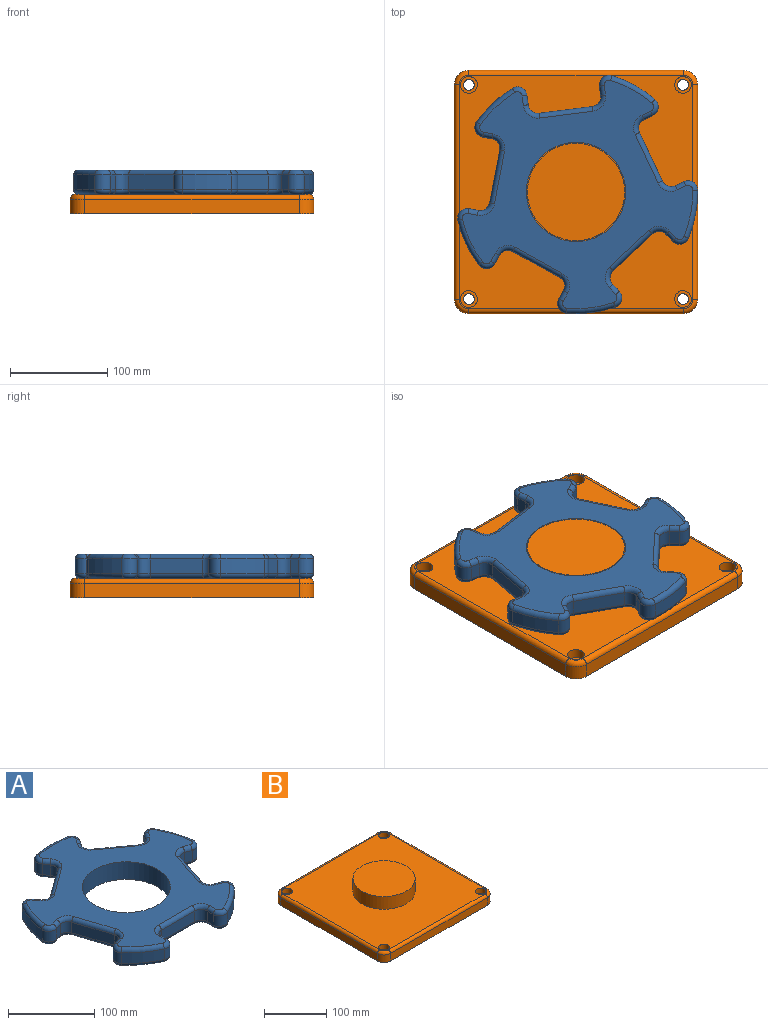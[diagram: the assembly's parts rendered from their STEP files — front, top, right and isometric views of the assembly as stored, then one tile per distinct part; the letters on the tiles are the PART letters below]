
ASSEMBLY  parts=2 mates=1
PART A: 123 faces, bbox 268.9x258.5x25 mm
  f0: plane 238.57x229.73mm, normal (0,0,1), area 21505.7mm2, adj f6,f43,f44,f45,f46,f47,f48,f49
  f1: plane 238.57x229.73mm, normal (0,0,-1), area 21505.7mm2, adj f6,f83,f84,f85,f86,f87,f88,f89
  f2: cylinder r=125mm len=40.68mm, axis (0,0,-1), area 759.5mm2, adj f13,f42,f51,f91
  f3: cylinder r=125mm len=47.82mm, axis (0,0,-1), area 759.5mm2, adj f35,f41,f67,f107
  f4: cylinder r=125mm len=50.29mm, axis (0,0,-1), area 759.5mm2, adj f28,f34,f82,f122
  f5: cylinder r=125mm len=47.82mm, axis (0,0,-1), area 759.5mm2, adj f21,f27,f66,f106
  f6: cylinder r=51mm len=102mm, axis (0,0,-1), area 8011.1mm2, adj f0,f1
  f7: cylinder r=125mm len=40.68mm, axis (0,0,-1), area 759.5mm2, adj f14,f20,f50,f90
  f8: plane 15x9.73mm, normal (-1,0,0), area 146mm2, adj f11,f14,f46,f86
  f9: plane 55x15mm, normal (0,-1,0), area 825mm2, adj f11,f12,f43,f83
  f10: plane 15x9.73mm, normal (1,0,0), area 146mm2, adj f12,f13,f47,f87
  f11: cylinder r=10mm len=15mm, axis (0,0,-1), area 235.6mm2, adj f8,f9,f44,f84
  f12: cylinder r=10mm len=15mm, axis (0,0,-1), area 235.6mm2, adj f9,f10,f45,f85
  f13: cylinder r=10mm len=15mm, axis (0,0,-1), area 299.5mm2, adj f2,f10,f49,f89
  f14: cylinder r=10mm len=15mm, axis (0,0,-1), area 299.5mm2, adj f7,f8,f48,f88
  f15: plane 15x9.26mm, normal (-0.31,-0.95,0), area 146mm2, adj f18,f21,f62,f102
  f16: plane 52.31x17mm, normal (0.95,-0.31,0), area 825mm2, adj f18,f19,f58,f98
  f17: plane 15x9.26mm, normal (0.31,0.95,0), area 146mm2, adj f19,f20,f54,f94
  f18: cylinder r=10mm len=15mm, axis (0,0,-1), area 235.6mm2, adj f15,f16,f60,f100
  f19: cylinder r=10mm len=15mm, axis (0,0,-1), area 235.6mm2, adj f16,f17,f56,f96
  f20: cylinder r=10mm len=16.25mm, axis (0,0,-1), area 299.5mm2, adj f7,f17,f52,f92
  f21: cylinder r=10mm len=15mm, axis (0,0,-1), area 299.5mm2, adj f5,f15,f64,f104
  f22: plane 15x7.87mm, normal (0.81,-0.59,0), area 146mm2, adj f25,f28,f78,f118
  f23: plane 44.5x32.33mm, normal (0.59,0.81,0), area 825mm2, adj f25,f26,f74,f114
  f24: plane 15x7.87mm, normal (-0.81,0.59,0), area 146mm2, adj f26,f27,f70,f110
  f25: cylinder r=10mm len=15mm, axis (0,0,-1), area 235.6mm2, adj f22,f23,f76,f116
  f26: cylinder r=10mm len=15mm, axis (0,0,-1), area 235.6mm2, adj f23,f24,f72,f112
  f27: cylinder r=10mm len=16.78mm, axis (0,0,-1), area 299.5mm2, adj f5,f24,f68,f108
  f28: cylinder r=10mm len=15.67mm, axis (0,0,-1), area 299.5mm2, adj f4,f22,f80,f120
  f29: plane 15x7.87mm, normal (0.81,0.59,0), area 146mm2, adj f32,f35,f71,f111
  f30: plane 44.5x32.33mm, normal (-0.59,0.81,0), area 825mm2, adj f32,f33,f75,f115
  f31: plane 15x7.87mm, normal (-0.81,-0.59,0), area 146mm2, adj f33,f34,f79,f119
  f32: cylinder r=10mm len=15mm, axis (0,0,-1), area 235.6mm2, adj f29,f30,f73,f113
  f33: cylinder r=10mm len=15mm, axis (0,0,-1), area 235.6mm2, adj f30,f31,f77,f117
  f34: cylinder r=10mm len=15.67mm, axis (0,0,-1), area 299.5mm2, adj f4,f31,f81,f121
  f35: cylinder r=10mm len=16.78mm, axis (0,0,-1), area 299.5mm2, adj f3,f29,f69,f109
  f36: plane 15x9.26mm, normal (-0.31,0.95,0), area 146mm2, adj f39,f42,f55,f95
  f37: plane 52.31x17mm, normal (-0.95,-0.31,0), area 825mm2, adj f39,f40,f59,f99
  f38: plane 15x9.26mm, normal (0.31,-0.95,0), area 146mm2, adj f40,f41,f63,f103
  f39: cylinder r=10mm len=15mm, axis (0,0,-1), area 235.6mm2, adj f36,f37,f57,f97
  f40: cylinder r=10mm len=15mm, axis (0,0,-1), area 235.6mm2, adj f37,f38,f61,f101
  f41: cylinder r=10mm len=15mm, axis (0,0,-1), area 299.5mm2, adj f3,f38,f65,f105
  f42: cylinder r=10mm len=16.25mm, axis (0,0,-1), area 299.5mm2, adj f2,f36,f53,f93
  f43: cylinder r=5mm len=55mm, axis (1,0,0), area 432mm2, adj f0,f9,f44,f45
  f44: torus R=15mm, axis (0,0,1), area 145.8mm2, adj f0,f11,f43,f46
  f45: torus R=15mm, axis (0,0,1), area 145.8mm2, adj f0,f12,f43,f47
  f46: cylinder r=5mm len=9.73mm, axis (0,-1,0), area 76.4mm2, adj f0,f8,f44,f48
  f47: cylinder r=5mm len=9.73mm, axis (0,1,0), area 76.4mm2, adj f0,f10,f45,f49
  f48: torus R=5mm, axis (0,0,1), area 128.3mm2, adj f0,f14,f46,f50
  f49: torus R=5mm, axis (0,0,1), area 128.3mm2, adj f0,f13,f47,f51
  f50: torus R=120mm, axis (0,0,1), area 391.9mm2, adj f0,f7,f48,f52
  f51: torus R=120mm, axis (0,0,1), area 391.9mm2, adj f0,f2,f49,f53
  f52: torus R=5mm, axis (0,0,1), area 128.3mm2, adj f0,f20,f50,f54
  f53: torus R=5mm, axis (0,0,1), area 128.3mm2, adj f0,f42,f51,f55
  f54: cylinder r=5mm len=10.8mm, axis (-0.95,0.31,0), area 76.4mm2, adj f0,f17,f52,f56
  f55: cylinder r=5mm len=10.8mm, axis (-0.95,-0.31,0), area 76.4mm2, adj f0,f36,f53,f57
  f56: torus R=15mm, axis (0,0,1), area 145.8mm2, adj f0,f19,f54,f58
  f57: torus R=15mm, axis (0,0,1), area 145.8mm2, adj f0,f39,f55,f59
  f58: cylinder r=5mm len=53.85mm, axis (0.31,0.95,0), area 432mm2, adj f0,f16,f56,f60
  f59: cylinder r=5mm len=53.85mm, axis (0.31,-0.95,0), area 432mm2, adj f0,f37,f57,f61
  f60: torus R=15mm, axis (0,0,1), area 145.8mm2, adj f0,f18,f58,f62
  f61: torus R=15mm, axis (0,0,1), area 145.8mm2, adj f0,f40,f59,f63
  f62: cylinder r=5mm len=10.8mm, axis (0.95,-0.31,0), area 76.4mm2, adj f0,f15,f60,f64
  f63: cylinder r=5mm len=10.8mm, axis (0.95,0.31,0), area 76.4mm2, adj f0,f38,f61,f65
  f64: torus R=5mm, axis (0,0,1), area 128.3mm2, adj f0,f21,f62,f66
  f65: torus R=5mm, axis (0,0,1), area 128.3mm2, adj f0,f41,f63,f67
  f66: torus R=120mm, axis (0,0,1), area 391.9mm2, adj f0,f5,f64,f68
  f67: torus R=120mm, axis (0,0,1), area 391.9mm2, adj f0,f3,f65,f69
  f68: torus R=5mm, axis (0,0,1), area 128.3mm2, adj f0,f27,f66,f70
  f69: torus R=5mm, axis (0,0,1), area 128.3mm2, adj f0,f35,f67,f71
  f70: cylinder r=5mm len=10.81mm, axis (-0.59,-0.81,0), area 76.4mm2, adj f0,f24,f68,f72
  f71: cylinder r=5mm len=10.81mm, axis (-0.59,0.81,0), area 76.4mm2, adj f0,f29,f69,f73
  f72: torus R=15mm, axis (0,0,1), area 145.8mm2, adj f0,f26,f70,f74
  f73: torus R=15mm, axis (0,0,1), area 145.8mm2, adj f0,f32,f71,f75
  f74: cylinder r=5mm len=47.44mm, axis (-0.81,0.59,0), area 432mm2, adj f0,f23,f72,f76
  f75: cylinder r=5mm len=47.44mm, axis (-0.81,-0.59,0), area 432mm2, adj f0,f30,f73,f77
  f76: torus R=15mm, axis (0,0,1), area 145.8mm2, adj f0,f25,f74,f78
  f77: torus R=15mm, axis (0,0,1), area 145.8mm2, adj f0,f33,f75,f79
  f78: cylinder r=5mm len=10.81mm, axis (0.59,0.81,0), area 76.4mm2, adj f0,f22,f76,f80
  f79: cylinder r=5mm len=10.81mm, axis (0.59,-0.81,0), area 76.4mm2, adj f0,f31,f77,f81
  f80: torus R=5mm, axis (0,0,1), area 128.3mm2, adj f0,f28,f78,f82
  f81: torus R=5mm, axis (0,0,1), area 128.3mm2, adj f0,f34,f79,f82
  f82: torus R=120mm, axis (0,0,1), area 391.9mm2, adj f0,f4,f80,f81
  f83: cylinder r=5mm len=55mm, axis (-1,0,0), area 432mm2, adj f1,f9,f84,f85
  f84: torus R=15mm, axis (0,0,1), area 145.8mm2, adj f1,f11,f83,f86
  f85: torus R=15mm, axis (0,0,1), area 145.8mm2, adj f1,f12,f83,f87
  f86: cylinder r=5mm len=9.73mm, axis (0,1,0), area 76.4mm2, adj f1,f8,f84,f88
  f87: cylinder r=5mm len=9.73mm, axis (0,-1,0), area 76.4mm2, adj f1,f10,f85,f89
  f88: torus R=5mm, axis (0,0,1), area 128.3mm2, adj f1,f14,f86,f90
  f89: torus R=5mm, axis (0,0,1), area 128.3mm2, adj f1,f13,f87,f91
  f90: torus R=120mm, axis (0,0,1), area 391.9mm2, adj f1,f7,f88,f92
  f91: torus R=120mm, axis (0,0,1), area 391.9mm2, adj f1,f2,f89,f93
  f92: torus R=5mm, axis (0,0,1), area 128.3mm2, adj f1,f20,f90,f94
  f93: torus R=5mm, axis (0,0,1), area 128.3mm2, adj f1,f42,f91,f95
  f94: cylinder r=5mm len=10.8mm, axis (0.95,-0.31,0), area 76.4mm2, adj f1,f17,f92,f96
  f95: cylinder r=5mm len=10.8mm, axis (0.95,0.31,0), area 76.4mm2, adj f1,f36,f93,f97
  f96: torus R=15mm, axis (0,0,1), area 145.8mm2, adj f1,f19,f94,f98
  f97: torus R=15mm, axis (0,0,1), area 145.8mm2, adj f1,f39,f95,f99
  f98: cylinder r=5mm len=53.85mm, axis (-0.31,-0.95,0), area 432mm2, adj f1,f16,f96,f100
  f99: cylinder r=5mm len=53.85mm, axis (-0.31,0.95,0), area 432mm2, adj f1,f37,f97,f101
  f100: torus R=15mm, axis (0,0,1), area 145.8mm2, adj f1,f18,f98,f102
  f101: torus R=15mm, axis (0,0,1), area 145.8mm2, adj f1,f40,f99,f103
  f102: cylinder r=5mm len=10.8mm, axis (-0.95,0.31,0), area 76.4mm2, adj f1,f15,f100,f104
  f103: cylinder r=5mm len=10.8mm, axis (-0.95,-0.31,0), area 76.4mm2, adj f1,f38,f101,f105
  f104: torus R=5mm, axis (0,0,1), area 128.3mm2, adj f1,f21,f102,f106
  f105: torus R=5mm, axis (0,0,1), area 128.3mm2, adj f1,f41,f103,f107
  f106: torus R=120mm, axis (0,0,1), area 391.9mm2, adj f1,f5,f104,f108
  f107: torus R=120mm, axis (0,0,1), area 391.9mm2, adj f1,f3,f105,f109
  f108: torus R=5mm, axis (0,0,1), area 128.3mm2, adj f1,f27,f106,f110
  f109: torus R=5mm, axis (0,0,1), area 128.3mm2, adj f1,f35,f107,f111
  f110: cylinder r=5mm len=10.81mm, axis (0.59,0.81,0), area 76.4mm2, adj f1,f24,f108,f112
  f111: cylinder r=5mm len=10.81mm, axis (0.59,-0.81,0), area 76.4mm2, adj f1,f29,f109,f113
  f112: torus R=15mm, axis (0,0,1), area 145.8mm2, adj f1,f26,f110,f114
  f113: torus R=15mm, axis (0,0,1), area 145.8mm2, adj f1,f32,f111,f115
  f114: cylinder r=5mm len=47.44mm, axis (0.81,-0.59,0), area 432mm2, adj f1,f23,f112,f116
  f115: cylinder r=5mm len=47.44mm, axis (0.81,0.59,0), area 432mm2, adj f1,f30,f113,f117
  f116: torus R=15mm, axis (0,0,1), area 145.8mm2, adj f1,f25,f114,f118
  f117: torus R=15mm, axis (0,0,1), area 145.8mm2, adj f1,f33,f115,f119
  f118: cylinder r=5mm len=10.81mm, axis (-0.59,-0.81,0), area 76.4mm2, adj f1,f22,f116,f120
  f119: cylinder r=5mm len=10.81mm, axis (-0.59,0.81,0), area 76.4mm2, adj f1,f31,f117,f121
  f120: torus R=5mm, axis (0,0,1), area 128.3mm2, adj f1,f28,f118,f122
  f121: torus R=5mm, axis (0,0,1), area 128.3mm2, adj f1,f34,f119,f122
  f122: torus R=120mm, axis (0,0,1), area 391.9mm2, adj f1,f4,f120,f121
PART B: 32 faces, bbox 252.5x252.5x45 mm
  f0: plane 220x15mm, normal (1,0,0), area 3300mm2, adj f5,f8,f11,f27
  f1: plane 220x15mm, normal (0,1,0), area 3300mm2, adj f5,f8,f9,f31
  f2: plane 220x15mm, normal (-1,0,0), area 3300mm2, adj f5,f9,f10,f28
  f3: plane 220x15mm, normal (0,-1,0), area 3300mm2, adj f5,f10,f11,f24
  f4: plane 240x240mm, normal (0,0,1), area 48725.4mm2, adj f6,f14,f17,f20,f23,f24,f25,f26
  f5: plane 250x250mm, normal (0,0,-1), area 61926.7mm2, adj f0,f1,f2,f3,f8,f9,f10,f11
  f6: cylinder r=50mm len=100mm, axis (0,0,-1), area 7854mm2, adj f4,f7
  f7: plane 100x100mm, normal (0,0,1), area 7854mm2, adj f6
  f8: cylinder r=15mm len=15mm, axis (0,0,-1), area 353.4mm2, adj f0,f1,f5,f29
  f9: cylinder r=15mm len=15mm, axis (0,0,1), area 353.4mm2, adj f1,f2,f5,f30
  f10: cylinder r=15mm len=15mm, axis (0,0,-1), area 353.4mm2, adj f2,f3,f5,f26
  f11: cylinder r=15mm len=15mm, axis (0,0,1), area 353.4mm2, adj f0,f3,f5,f25
  f12: cylinder r=5.5mm len=11mm, axis (0,0,1), area 345.6mm2, adj f5,f13
  f13: plane 17.25x17.25mm, normal (0,0,1), area 138.7mm2, adj f12,f14
  f14: cylinder r=8.62mm len=17.25mm, axis (0,0,1), area 541.9mm2, adj f4,f13
  f15: cylinder r=5.5mm len=11mm, axis (0,0,1), area 345.6mm2, adj f5,f16
  f16: plane 17.25x17.25mm, normal (0,0,1), area 138.7mm2, adj f15,f17
  f17: cylinder r=8.62mm len=17.25mm, axis (0,0,1), area 541.9mm2, adj f4,f16
  f18: cylinder r=5.5mm len=11mm, axis (0,0,1), area 345.6mm2, adj f5,f19
  f19: plane 17.25x17.25mm, normal (0,0,1), area 138.7mm2, adj f18,f20
  f20: cylinder r=8.62mm len=17.25mm, axis (0,0,1), area 541.9mm2, adj f4,f19
  f21: cylinder r=5.5mm len=11mm, axis (0,0,1), area 345.6mm2, adj f5,f22
  f22: plane 17.25x17.25mm, normal (0,0,1), area 138.7mm2, adj f21,f23
  f23: cylinder r=8.62mm len=17.25mm, axis (0,0,1), area 541.9mm2, adj f4,f22
  f24: cylinder r=5mm len=220mm, axis (-1,0,0), area 1727.9mm2, adj f3,f4,f25,f26
  f25: torus R=10mm, axis (0,0,1), area 162.6mm2, adj f4,f11,f24,f27
  f26: torus R=10mm, axis (0,0,1), area 162.6mm2, adj f4,f10,f24,f28
  f27: cylinder r=5mm len=220mm, axis (0,-1,0), area 1727.9mm2, adj f0,f4,f25,f29
  f28: cylinder r=5mm len=220mm, axis (0,1,0), area 1727.9mm2, adj f2,f4,f26,f30
  f29: torus R=10mm, axis (0,0,1), area 162.6mm2, adj f4,f8,f27,f31
  f30: torus R=10mm, axis (0,0,1), area 162.6mm2, adj f4,f9,f28,f31
  f31: cylinder r=5mm len=220mm, axis (1,0,0), area 1727.9mm2, adj f1,f4,f29,f30
PLACE A rot(axis=(0,0,1),115.2deg) t=(0,0,0)mm
PLACE B at identity fixed
MATE revolute A.f2 <-> B.f6  axis (0,0,1) through (0,0,45)mm
